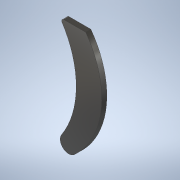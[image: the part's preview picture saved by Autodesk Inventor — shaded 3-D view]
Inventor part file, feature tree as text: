
AUTODESK INVENTOR PART (.ipt)
format: ipt  version: 2021 (Build 250183000, 183)  size: 118,784 bytes
history: native  units: in
note: dims shown in document units (in); Inventor stores cm internally (conversion verified against a paired STEP export)
features: extrude x2, sketch x2, fillet x1, projected_geometry x1
ambient origin geometry x8: Origin, YZ Plane, XZ Plane, XY Plane, X Axis, Y Axis, Z Axis, Center Point
bodies: Solid1 (feature_tree)
feature tree (6):
  extrude  "Extrusion1"  Depth=0.0394in
  extrude  "Extrusion2"  Depth=0.0157in
  fillet  "Fillet1"  [1 undecoded]
  sketch  "Sketch1"  dims[d3=0.0394in d4=0.0in d5=0.0591in]
  sketch  "Sketch2"  dims[d6=0.1378in d7=0.0in d8=0.0157in]
  projected_geometry  "Projected Loop1"
note: 1 required parameter value undecoded (feature->parameter linkage not recoverable at this tier; creation-order binding heuristic only, values carry confidence <= 0.55)
